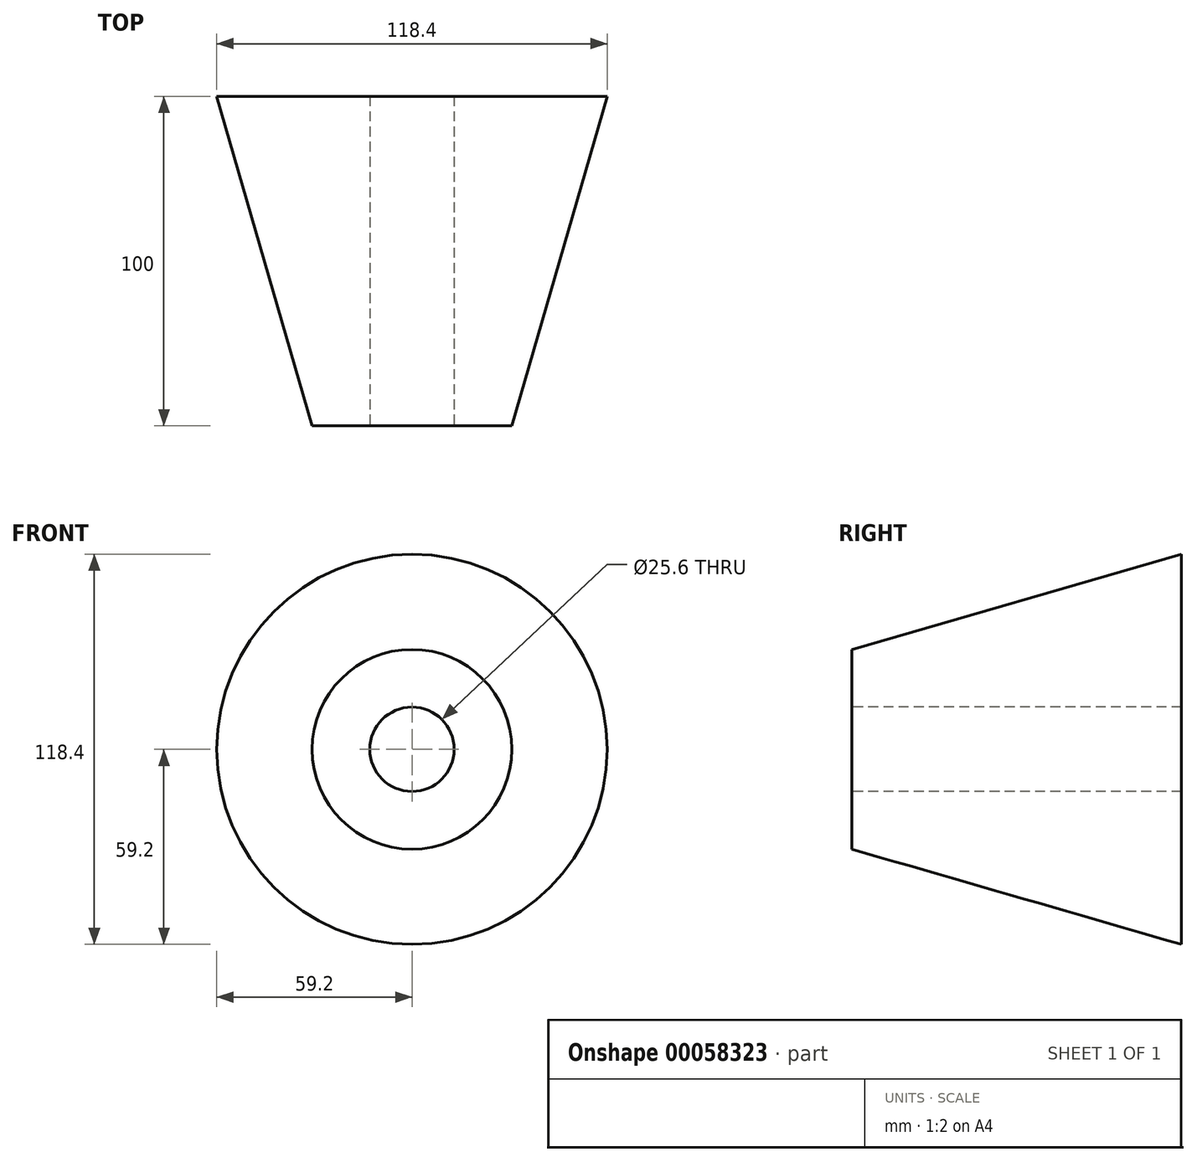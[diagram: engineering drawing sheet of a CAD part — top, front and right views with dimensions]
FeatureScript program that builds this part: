
annotation { "Feature Type Name" : "Feature", "Feature Type Description" : "" }
export const myFeature = defineFeature(function(context is Context, id is Id, definition is map)
    precondition{}
    {
        {
            var Q0;
            Q0=qCreatedBy(makeId("Front.planeOp"),FACE);
            var sketch = newSketch(context, id + "F0", { "sketchPlane" : qUnion([Q0])});
            skCircle(sketch, "E0", {"center": v(0, 0) * mm, "radius": 59.2 * mm});
            skSolve(sketch);
        }
        {
            var Q0;
            Q0=qCreatedBy(makeId("Front.planeOp"),FACE);
            cPlane(context, id + "F1", {"entities" : qUnion([Q0]), "cplaneType" : CPlaneType.OFFSET, "offset" : 100 * mm, "width" : 150 * mm, "height" : 150 * mm});
        }
        {
            var Q0;
            Q0=qCreatedBy(id+"F1.planeOp",FACE);
            var sketch = newSketch(context, id + "F2", { "sketchPlane" : qUnion([Q0])});
            skCircle(sketch, "E1", {"center": v(0, 0) * mm, "radius": 30.3 * mm});
            skSolve(sketch);
        }
        {
            var Q0;
            Q0=makeQuery(id+"F2.imprint","IMPRINT",FACE,{"disambiguationData":[TD([[makeQuery(id+"F2.imprint","IMPRINT",EDGE,{"derivedFrom":sQuery(id+"F2.wireOp",EDGE,"E1")}),1.0]])]});
            var Q1;
            Q1=makeQuery(id+"F0.imprint","IMPRINT",FACE,{"disambiguationData":[TD([[makeQuery(id+"F0.imprint","IMPRINT",EDGE,{"derivedFrom":sQuery(id+"F0.wireOp",EDGE,"E0")}),1.0]])]});
            loft(context, id + "F3", {"sheetProfilesArray" : [{ "sheetProfileEntities" : qUnion([Q0]) }, { "sheetProfileEntities" : qUnion([Q1]) }]});
        }
        {
            var Q0;
            Q0=makeQuery(id+"F3.opLoft","CAP_FACE",FACE,{"disambiguationData":[OSD([makeQuery(id+"F2.imprint","IMPRINT",FACE,{"disambiguationData":[TD([[makeQuery(id+"F2.imprint","IMPRINT",EDGE,{"derivedFrom":sQuery(id+"F2.wireOp",EDGE,"E1")}),1.0]])]})])],"isStart":true});
            var sketch = newSketch(context, id + "F4", { "sketchPlane" : qUnion([Q0])});
            skCircle(sketch, "E2", {"center": v(0, 0) * mm, "radius": 12.8 * mm});
            skSolve(sketch);
        }
        {
            var Q0;
            Q0=makeQuery(id+"F4.imprint","IMPRINT",FACE,{"disambiguationData":[TD([[makeQuery(id+"F4.imprint","IMPRINT",EDGE,{"derivedFrom":sQuery(id+"F4.wireOp",EDGE,"E2")}),1.0]])]});
            extrude(context, id + "F5", {"entities" : qUnion([Q0]), "operationType" : NewBodyOperationType.REMOVE, "endBound" : BoundingType.THROUGH_ALL, "oppositeDirection" : true, "depth" : 25 * mm});
        }
    });
